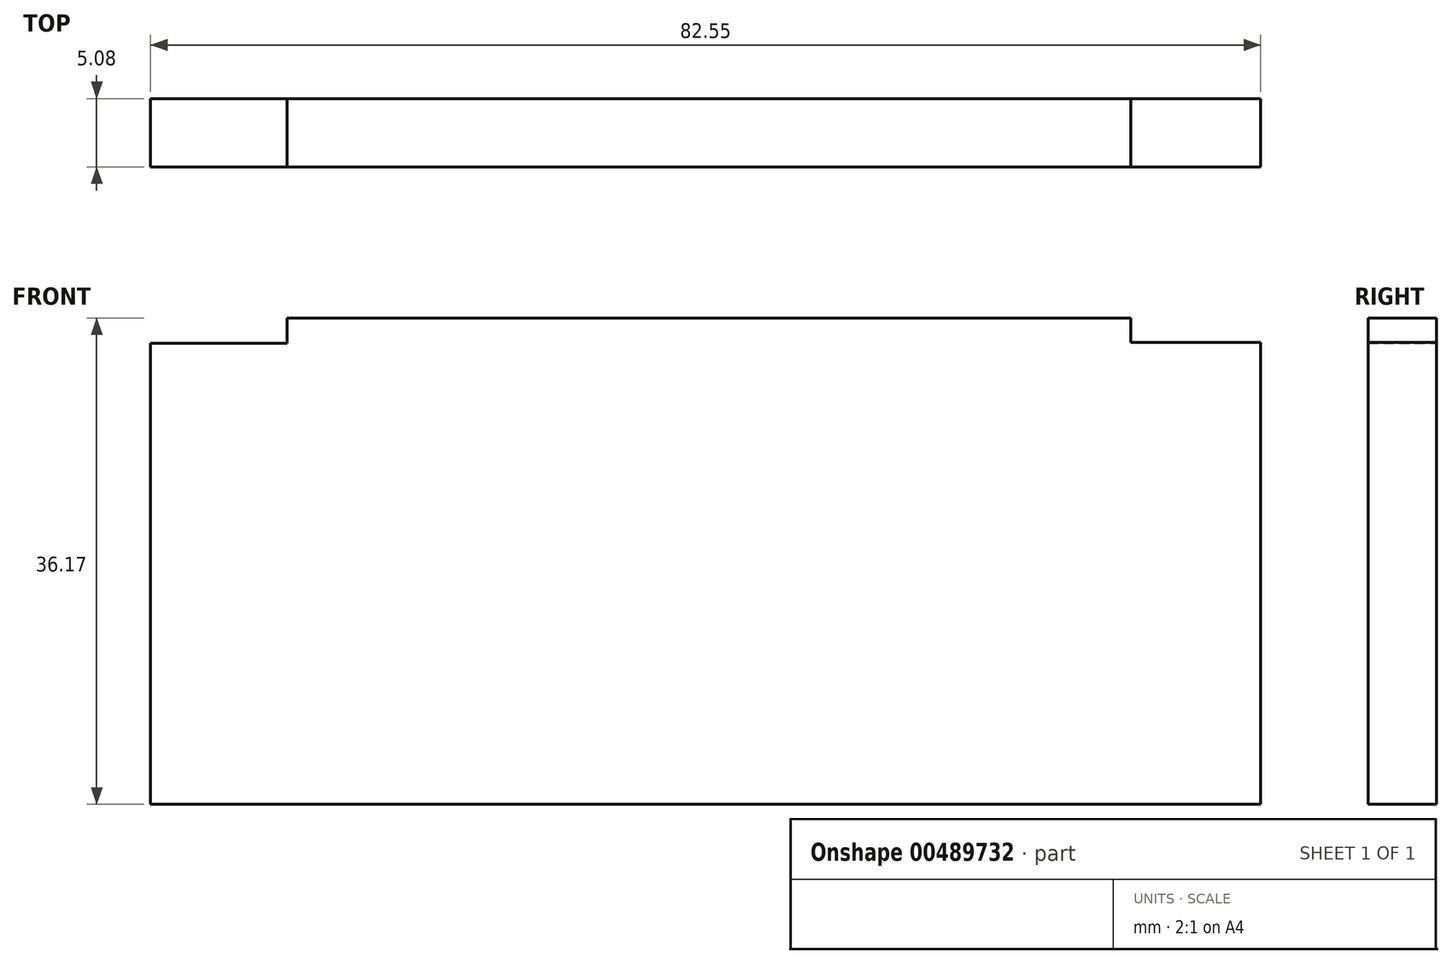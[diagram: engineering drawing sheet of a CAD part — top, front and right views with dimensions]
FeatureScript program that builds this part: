
annotation { "Feature Type Name" : "Feature", "Feature Type Description" : "" }
export const myFeature = defineFeature(function(context is Context, id is Id, definition is map)
    precondition{}
    {
        {
            var Q0;
            Q0=qCreatedBy(makeId("Front.planeOp"),FACE);
            var sketch = newSketch(context, id + "F0", { "sketchPlane" : qUnion([Q0])});
            skLineSegment(sketch, "E0.bottom", {"start": v(-20.46, 13) * mm, "end": v(42.28, 13) * mm});
            skLineSegment(sketch, "E0.top", {"start": v(-30.62, -23.18) * mm, "end": v(51.93, -23.18) * mm});
            skLineSegment(sketch, "E0.left", {"start": v(-30.62, 11.13) * mm, "end": v(-30.62, -23.18) * mm});
            skLineSegment(sketch, "E0.right", {"start": v(51.93, 11.17) * mm, "end": v(51.93, -23.18) * mm});
            skLineSegment(sketch, "E1.top", {"start": v(-30.62, 11.13) * mm, "end": v(-20.46, 11.13) * mm});
            skLineSegment(sketch, "E1.right", {"start": v(-20.46, 12.9) * mm, "end": v(-20.46, 11.13) * mm});
            skLineSegment(sketch, "E2.top", {"start": v(42.28, 11.17) * mm, "end": v(51.93, 11.17) * mm});
            skLineSegment(sketch, "E2.left", {"start": v(42.28, 12.95) * mm, "end": v(42.28, 11.17) * mm});
            skLineSegment(sketch, "E3", {"start": v(-20.46, 13) * mm, "end": v(-20.46, 12.9) * mm});
            skLineSegment(sketch, "E4", {"start": v(42.28, 13) * mm, "end": v(42.28, 12.95) * mm});
            skSolve(sketch);
        }
        {
            var Q0;
            Q0 = qSketchRegion(id + "F0", true);
            extrude(context, id + "F1", {"entities" : qUnion([Q0]), "depth" : 5.08 * mm});
        }
    });
